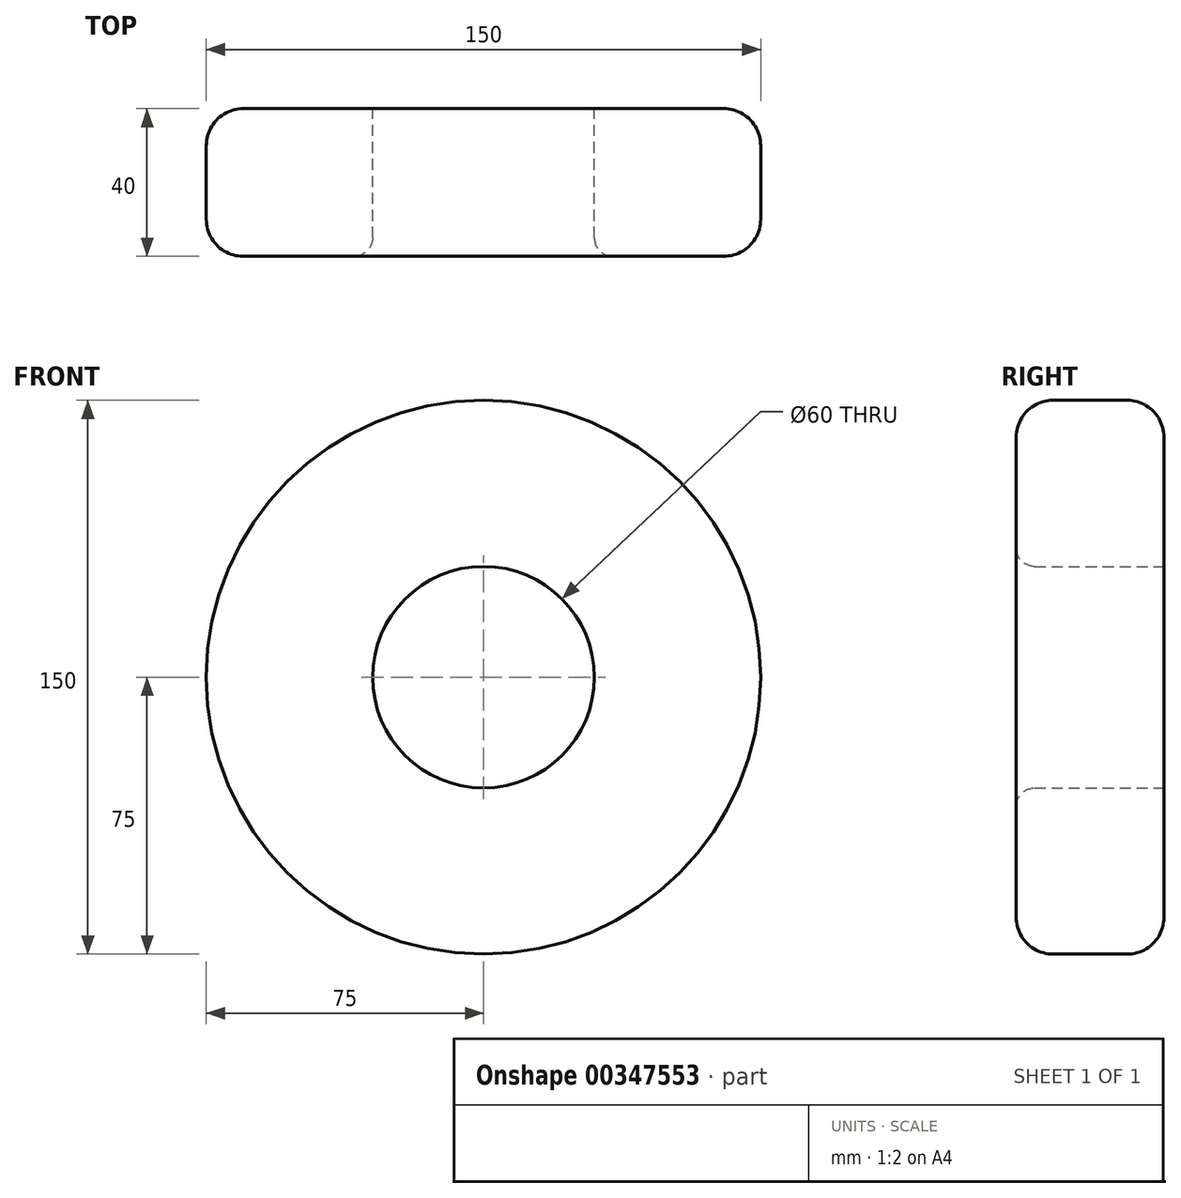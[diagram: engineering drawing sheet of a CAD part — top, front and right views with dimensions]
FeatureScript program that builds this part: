
annotation { "Feature Type Name" : "Feature", "Feature Type Description" : "" }
export const myFeature = defineFeature(function(context is Context, id is Id, definition is map)
    precondition{}
    {
        {
            var Q0;
            Q0=qCreatedBy(makeId("Front.planeOp"),FACE);
            var sketch = newSketch(context, id + "F0", { "sketchPlane" : qUnion([Q0])});
            skCircle(sketch, "E0", {"center": v(0, 0) * mm, "radius": 75 * mm});
            skSolve(sketch);
        }
        {
            var Q0;
            Q0=makeQuery(id+"F0.imprint","IMPRINT",FACE,{"disambiguationData":[TD([[makeQuery(id+"F0.imprint","IMPRINT",EDGE,{"derivedFrom":sQuery(id+"F0.wireOp",EDGE,"E0")}),1.0]])]});
            extrude(context, id + "F1", {"entities" : qUnion([Q0]), "depth" : 40 * mm});
        }
        {
            var Q0;
            Q0=makeQuery(id+"F1.opExtrude","CAP_EDGE",EDGE,{"disambiguationData":[OSD([sQuery(id+"F0.wireOp",EDGE,"E0")])],"isStart":false});
            fillet(context, id + "F2", {"entities" : qUnion([Q0]), "radius" : 10 * mm, "tangentPropagation" : true, "allowEdgeOverflow" : false});
        }
        {
            var Q0;
            Q0=makeQuery(id+"F1.opExtrude","CAP_EDGE",EDGE,{"disambiguationData":[OSD([sQuery(id+"F0.wireOp",EDGE,"E0")])],"isStart":true});
            fillet(context, id + "F3", {"entities" : qUnion([Q0]), "radius" : 10 * mm, "tangentPropagation" : true, "allowEdgeOverflow" : false});
        }
        {
            var Q0;
            Q0=makeQuery(id+"F1.opExtrude","CAP_FACE",FACE,{"disambiguationData":[OSD([sQuery(id+"F0.wireOp",EDGE,"E0")])],"isStart":true});
            var sketch = newSketch(context, id + "F4", { "sketchPlane" : qUnion([Q0])});
            skCircle(sketch, "E1", {"center": v(0, 0) * mm, "radius": 30 * mm});
            skSolve(sketch);
        }
        {
            var Q0;
            Q0=makeQuery(id+"F4.imprint","IMPRINT",FACE,{"disambiguationData":[TD([[makeQuery(id+"F4.imprint","IMPRINT",EDGE,{"derivedFrom":sQuery(id+"F4.wireOp",EDGE,"E1")}),1.0]])]});
            extrude(context, id + "F5", {"entities" : qUnion([Q0]), "operationType" : NewBodyOperationType.REMOVE, "oppositeDirection" : true, "depth" : 45 * mm});
        }
        {
            var Q0;
            Q0=makeQuery(id+"F5.boolean.opBoolean","INTERSECT",EDGE,{"derivedFrom":[makeQuery(id+"F1.opExtrude","CAP_FACE",FACE,{"disambiguationData":[OSD([sQuery(id+"F0.wireOp",EDGE,"E0")])],"isStart":false}),makeQuery(id+"F5.opExtrude","SWEPT_FACE",FACE,{"disambiguationData":[OSD([sQuery(id+"F4.wireOp",EDGE,"E1")])]})]});
            var Q1;
            Q1=makeQuery(id+"F5.boolean.opBoolean","COPY",EDGE,{"derivedFrom":makeQuery(id+"F5.opExtrude","CAP_EDGE",EDGE,{"disambiguationData":[OSD([sQuery(id+"F4.wireOp",EDGE,"E1")])],"isStart":true})});
            fillet(context, id + "F6", {"entities" : qUnion([Q0, Q1]), "radius" : 5 * mm, "tangentPropagation" : true, "allowEdgeOverflow" : false});
        }
    });
